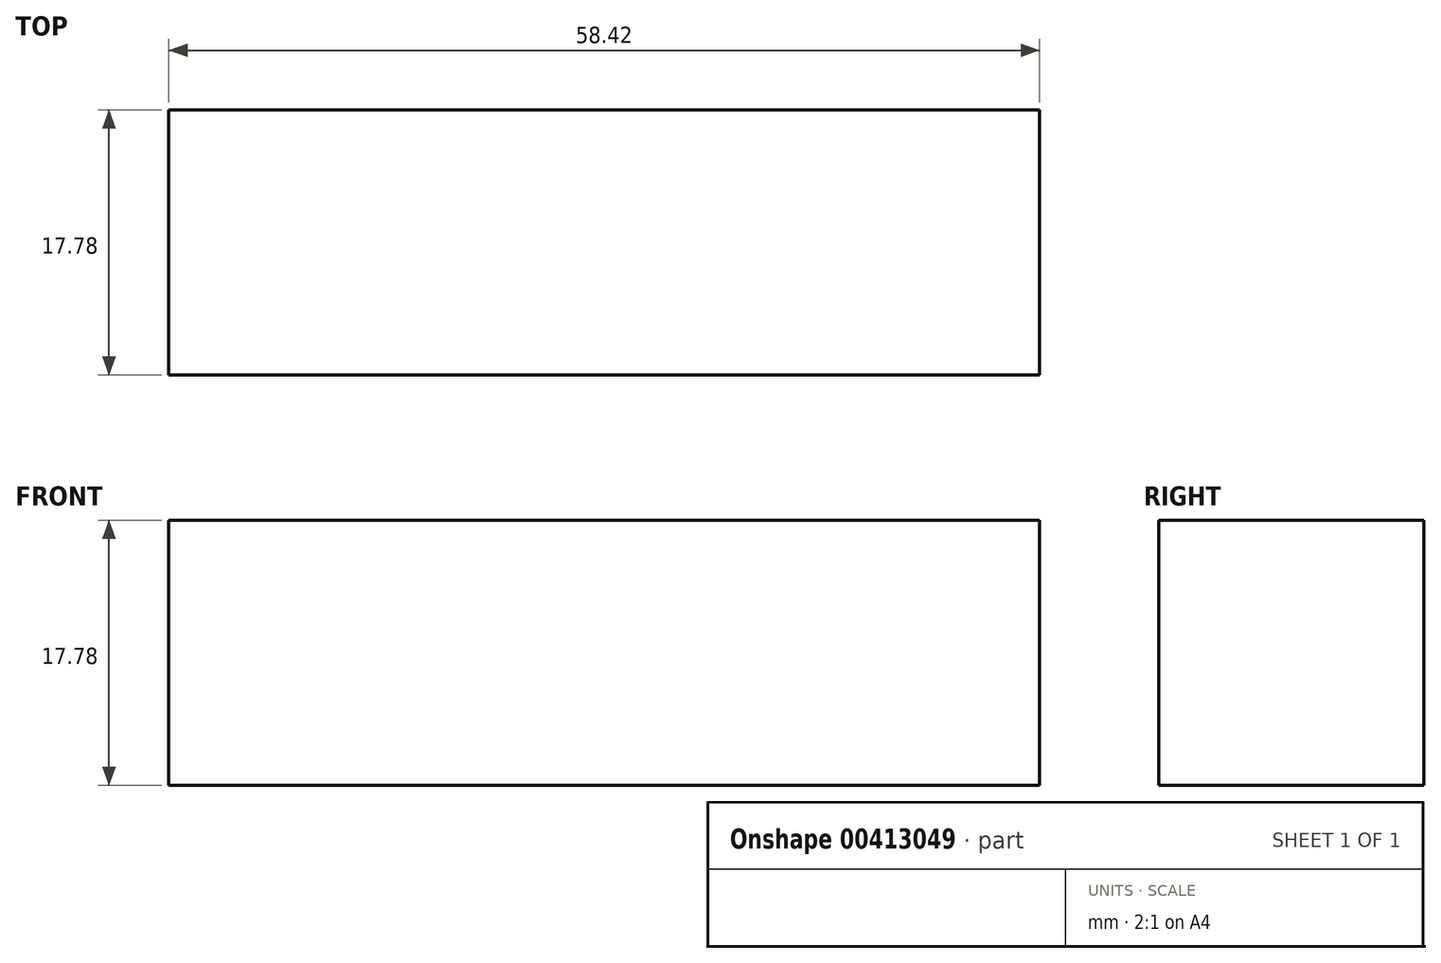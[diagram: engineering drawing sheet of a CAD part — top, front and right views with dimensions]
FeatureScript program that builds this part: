
annotation { "Feature Type Name" : "Feature", "Feature Type Description" : "" }
export const myFeature = defineFeature(function(context is Context, id is Id, definition is map)
    precondition{}
    {
        {
            var Q0;
            Q0=qCreatedBy(makeId("Front.planeOp"),FACE);
            var sketch = newSketch(context, id + "F0", { "sketchPlane" : qUnion([Q0])});
            skLineSegment(sketch, "E0.bottom", {"start": v(0, 0) * mm, "end": v(58.42, 0) * mm});
            skLineSegment(sketch, "E0.top", {"start": v(0, 17.78) * mm, "end": v(58.42, 17.78) * mm});
            skLineSegment(sketch, "E0.left", {"start": v(0, 0) * mm, "end": v(0, 17.78) * mm});
            skLineSegment(sketch, "E0.right", {"start": v(58.42, 0) * mm, "end": v(58.42, 17.78) * mm});
            skSolve(sketch);
        }
        {
            var Q0;
            Q0 = qSketchRegion(id + "F0", true);
            extrude(context, id + "F1", {"entities" : qUnion([Q0]), "depth" : 17.78 * mm});
        }
    });
